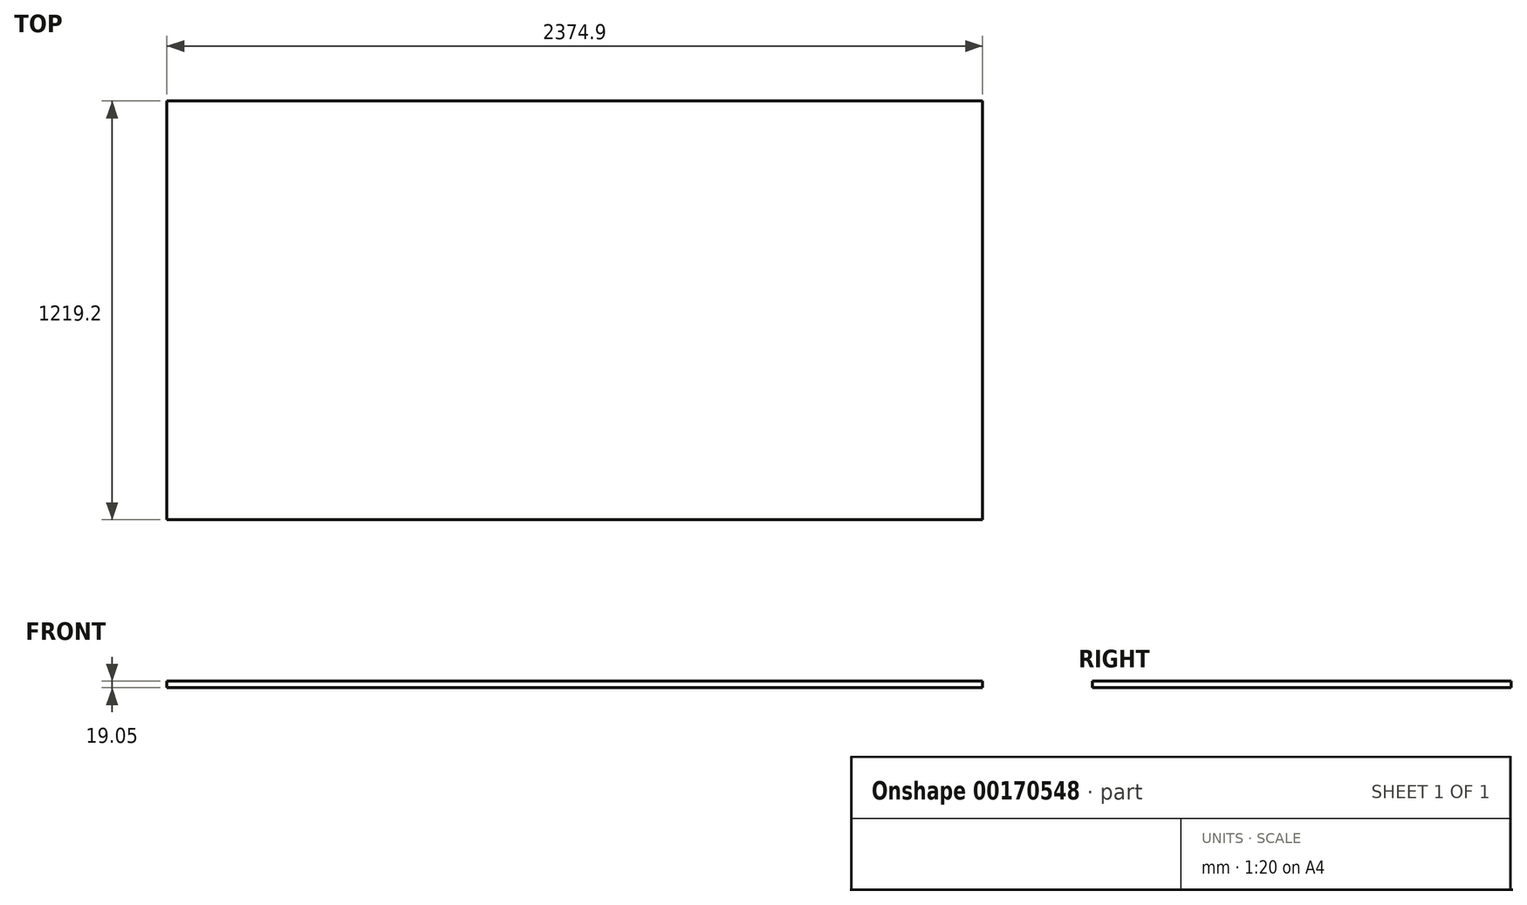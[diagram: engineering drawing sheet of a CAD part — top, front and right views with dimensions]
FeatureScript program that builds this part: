
annotation { "Feature Type Name" : "Feature", "Feature Type Description" : "" }
export const myFeature = defineFeature(function(context is Context, id is Id, definition is map)
    precondition{}
    {
        {
            var Q0;
            Q0=qCreatedBy(makeId("Top.planeOp"),FACE);
            var sketch = newSketch(context, id + "F0", { "sketchPlane" : qUnion([Q0])});
            skLineSegment(sketch, "E0.bottom", {"start": v(0, 0) * mm, "end": v(2374.9, 0) * mm});
            skLineSegment(sketch, "E0.top", {"start": v(0, 1219.2) * mm, "end": v(2374.9, 1219.2) * mm});
            skLineSegment(sketch, "E0.left", {"start": v(0, 0) * mm, "end": v(0, 1219.2) * mm});
            skLineSegment(sketch, "E0.right", {"start": v(2374.9, 0) * mm, "end": v(2374.9, 1219.2) * mm});
            skSolve(sketch);
        }
        {
            var Q0;
            Q0=makeQuery(id+"F0.imprint","IMPRINT",FACE,{"disambiguationData":[TD([[makeQuery(id+"F0.imprint","IMPRINT",EDGE,{"derivedFrom":sQuery(id+"F0.wireOp",EDGE,"E0.bottom")}),1.0]])]});
            extrude(context, id + "F1", {"entities" : qUnion([Q0]), "depth" : 19.05 * mm});
        }
    });
